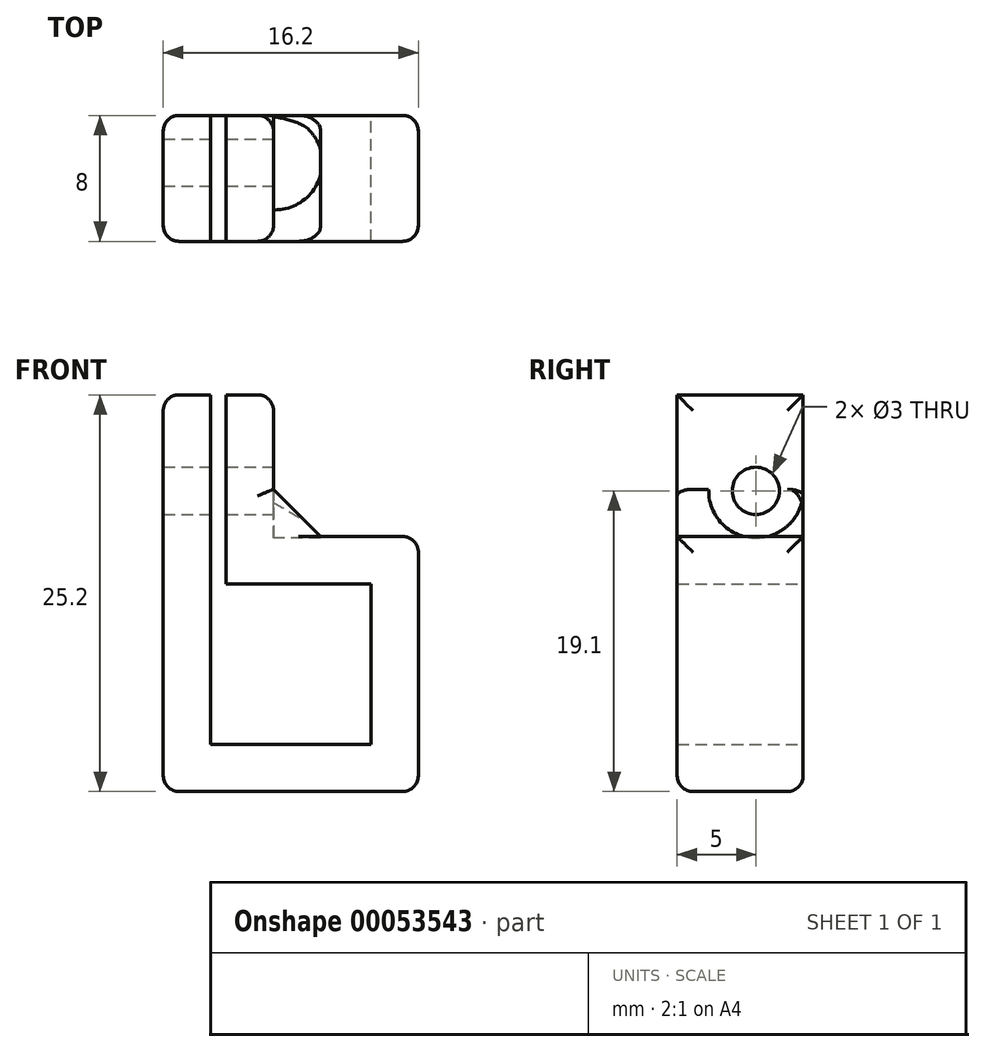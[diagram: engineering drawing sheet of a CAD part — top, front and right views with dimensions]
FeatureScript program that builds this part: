
annotation { "Feature Type Name" : "Feature", "Feature Type Description" : "" }
export const myFeature = defineFeature(function(context is Context, id is Id, definition is map)
    precondition{}
    {
        {
            var Q0;
            Q0=qCreatedBy(makeId("Front.planeOp"),FACE);
            var sketch = newSketch(context, id + "F0", { "sketchPlane" : qUnion([Q0])});
            skLineSegment(sketch, "E0.rect.bottom", {"start": v(5.1, -5.1) * mm, "end": v(-5.1, -5.1) * mm});
            skLineSegment(sketch, "E0.rect.top", {"start": v(5.1, 5.1) * mm, "end": v(-4.1, 5.1) * mm});
            skLineSegment(sketch, "E0.rect.left", {"start": v(5.1, -5.1) * mm, "end": v(5.1, 5.1) * mm});
            skLineSegment(sketch, "E0.rect.right", {"start": v(-5.1, -5.1) * mm, "end": v(-5.1, 5.1) * mm});
            skPoint(sketch, "E0.rect.middle", {"position": v(0, 0) * mm});
            skLineSegment(sketch, "E1.0", {"start": v(8.1, 8.1) * mm, "end": v(-1.1, 8.1) * mm});
            skLineSegment(sketch, "E1.1", {"start": v(8.1, -8.1) * mm, "end": v(8.1, 8.1) * mm});
            skLineSegment(sketch, "E1.2", {"start": v(8.1, -8.1) * mm, "end": v(-8.1, -8.1) * mm});
            skLineSegment(sketch, "E1.3", {"start": v(-8.1, -8.1) * mm, "end": v(-8.1, 8.1) * mm});
            skLineSegment(sketch, "E2", {"start": v(-8.1, 8.1) * mm, "end": v(-8.1, 17.1) * mm});
            skLineSegment(sketch, "E3", {"start": v(-8.1, 17.1) * mm, "end": v(-5.1, 17.1) * mm});
            skLineSegment(sketch, "E4", {"start": v(-5.1, 17.1) * mm, "end": v(-5.1, 8.1) * mm});
            skLineSegment(sketch, "E5", {"start": v(-4.1, 8.1) * mm, "end": v(-4.1, 17.1) * mm});
            skLineSegment(sketch, "E6", {"start": v(-4.1, 17.1) * mm, "end": v(-1.1, 17.1) * mm});
            skLineSegment(sketch, "E7", {"start": v(-1.1, 17.1) * mm, "end": v(-1.1, 8.1) * mm});
            skLineSegment(sketch, "E8", {"start": v(-5.1, 5.1) * mm, "end": v(-5.1, 8.1) * mm});
            skLineSegment(sketch, "E9", {"start": v(-4.1, 8.1) * mm, "end": v(-4.1, 5.1) * mm});
            skSolve(sketch);
        }
        {
            var Q0;
            Q0=qSketchRegion(id+"F0",true);
            extrude(context, id + "F1", {"entities" : qUnion([Q0]), "depth" : 8 * mm});
        }
        {
            var Q0;
            Q0=makeQuery(id+"F1.opExtrude","SWEPT_FACE",FACE,{"disambiguationData":[OSD([sQuery(id+"F0.wireOp",EDGE,"E7")])]});
            var sketch = newSketch(context, id + "F2", { "sketchPlane" : qUnion([Q0])});
            skCircle(sketch, "E10", {"center": v(-3, 11) * mm, "radius": 1.5 * mm});
            skPoint(sketch, "E10.centerSnap0", {"position": v(-7, 11) * mm});
            skPoint(sketch, "E10.centerSnap1", {"position": v(-3, 15.5) * mm});
            skSolve(sketch);
        }
        {
            var Q0;
            Q0=qSketchRegion(id+"F2",true);
            extrude(context, id + "F3", {"entities" : qUnion([Q0]), "operationType" : NewBodyOperationType.REMOVE, "endBound" : BoundingType.THROUGH_ALL, "oppositeDirection" : true, "depth" : 25 * mm});
        }
        {
            var Q0;
            Q0=makeQuery(id+"F1.opExtrude","SWEPT_EDGE",EDGE,{"disambiguationData":[OSD([sQuery(id+"F0.wireOp",EDGE,"E1.0"),sQuery(id+"F0.wireOp",EDGE,"E7")])]});
            chamfer(context, id + "F4", {"entities" : qUnion([Q0]), "width" : 3 * mm, "tangentPropagation" : true});
        }
        {
            var Q0;
            Q0=makeQuery(id+"F1.opExtrude","SWEPT_FACE",FACE,{"disambiguationData":[OSD([sQuery(id+"F0.wireOp",EDGE,"E1.1")])]});
            var Q1;
            Q1=makeQuery(id+"F1.opExtrude","SWEPT_FACE",FACE,{"disambiguationData":[OSD([sQuery(id+"F0.wireOp",EDGE,"E1.2")])]});
            var Q2;
            Q2=makeQuery(id+"F1.opExtrude","SWEPT_EDGE",EDGE,{"disambiguationData":[OSD([sQuery(id+"F0.wireOp",EDGE,"E2"),sQuery(id+"F0.wireOp",EDGE,"E3")])]});
            var Q3;
            Q3=makeQuery(id+"F1.opExtrude","CAP_EDGE",EDGE,{"disambiguationData":[OSD([sQuery(id+"F0.wireOp",EDGE,"E1.3"),sQuery(id+"F0.wireOp",EDGE,"E2")])],"isStart":true});
            var Q4;
            Q4=makeQuery(id+"F1.opExtrude","CAP_EDGE",EDGE,{"disambiguationData":[OSD([sQuery(id+"F0.wireOp",EDGE,"E1.3"),sQuery(id+"F0.wireOp",EDGE,"E2")])],"isStart":false});
            var Q5;
            Q5=makeQuery(id+"F1.opExtrude","SWEPT_EDGE",EDGE,{"disambiguationData":[OSD([sQuery(id+"F0.wireOp",EDGE,"E6"),sQuery(id+"F0.wireOp",EDGE,"E7")])]});
            var Q6;
            Q6=makeQuery(id+"F1.opExtrude","CAP_EDGE",EDGE,{"disambiguationData":[OSD([sQuery(id+"F0.wireOp",EDGE,"E7")])],"isStart":true});
            var Q7;
            Q7=makeQuery(id+"F1.opExtrude","CAP_EDGE",EDGE,{"disambiguationData":[OSD([sQuery(id+"F0.wireOp",EDGE,"E7")])],"isStart":false});
            fillet(context, id + "F5", {"entities" : qUnion([Q0, Q1, Q2, Q3, Q4, Q5, Q6, Q7]), "radius" : 1 * mm, "tangentPropagation" : true, "allowEdgeOverflow" : false});
        }
        {
            var Q0;
            {var subQ0=sQuery(id+"F0.wireOp",EDGE,"E7");var subQ1=sQuery(id+"F0.wireOp",EDGE,"E1.0");Q0=makeQuery(id+"F4.opChamfer","BLEND_EDGE",EDGE,{"blendedFrom":[makeQuery(id+"F1.opExtrude","SWEPT_EDGE",EDGE,{"disambiguationData":[OSD([subQ1,subQ0])]}),makeQuery(id+"F1.opExtrude","CAP_FACE",FACE,{"disambiguationData":[OSD([sQuery(id+"F0.wireOp",EDGE,"E0.rect.bottom"),sQuery(id+"F0.wireOp",EDGE,"E0.rect.top"),sQuery(id+"F0.wireOp",EDGE,"E0.rect.left"),sQuery(id+"F0.wireOp",EDGE,"E0.rect.right"),subQ1,sQuery(id+"F0.wireOp",EDGE,"E1.1"),sQuery(id+"F0.wireOp",EDGE,"E1.2"),sQuery(id+"F0.wireOp",EDGE,"E1.3"),sQuery(id+"F0.wireOp",EDGE,"E2"),sQuery(id+"F0.wireOp",EDGE,"E3"),sQuery(id+"F0.wireOp",EDGE,"E4"),sQuery(id+"F0.wireOp",EDGE,"E5"),sQuery(id+"F0.wireOp",EDGE,"E6"),subQ0,sQuery(id+"F0.wireOp",EDGE,"E8"),sQuery(id+"F0.wireOp",EDGE,"E9")])],"isStart":true})],"blendedInto":[makeQuery(id+"F1.opExtrude","CAP_FACE",FACE,{"disambiguationData":[OSD([sQuery(id+"F0.wireOp",EDGE,"E0.rect.bottom"),sQuery(id+"F0.wireOp",EDGE,"E0.rect.top"),sQuery(id+"F0.wireOp",EDGE,"E0.rect.left"),sQuery(id+"F0.wireOp",EDGE,"E0.rect.right"),subQ1,sQuery(id+"F0.wireOp",EDGE,"E1.1"),sQuery(id+"F0.wireOp",EDGE,"E1.2"),sQuery(id+"F0.wireOp",EDGE,"E1.3"),sQuery(id+"F0.wireOp",EDGE,"E2"),sQuery(id+"F0.wireOp",EDGE,"E3"),sQuery(id+"F0.wireOp",EDGE,"E4"),sQuery(id+"F0.wireOp",EDGE,"E5"),sQuery(id+"F0.wireOp",EDGE,"E6"),subQ0,sQuery(id+"F0.wireOp",EDGE,"E8"),sQuery(id+"F0.wireOp",EDGE,"E9")])],"isStart":true})]});}
            var Q1;
            {var subQ0=sQuery(id+"F0.wireOp",EDGE,"E7");var subQ1=sQuery(id+"F0.wireOp",EDGE,"E1.0");Q1=makeQuery(id+"F4.opChamfer","BLEND_EDGE",EDGE,{"blendedFrom":[makeQuery(id+"F1.opExtrude","SWEPT_EDGE",EDGE,{"disambiguationData":[OSD([subQ1,subQ0])]}),makeQuery(id+"F1.opExtrude","CAP_FACE",FACE,{"disambiguationData":[OSD([sQuery(id+"F0.wireOp",EDGE,"E0.rect.bottom"),sQuery(id+"F0.wireOp",EDGE,"E0.rect.top"),sQuery(id+"F0.wireOp",EDGE,"E0.rect.left"),sQuery(id+"F0.wireOp",EDGE,"E0.rect.right"),subQ1,sQuery(id+"F0.wireOp",EDGE,"E1.1"),sQuery(id+"F0.wireOp",EDGE,"E1.2"),sQuery(id+"F0.wireOp",EDGE,"E1.3"),sQuery(id+"F0.wireOp",EDGE,"E2"),sQuery(id+"F0.wireOp",EDGE,"E3"),sQuery(id+"F0.wireOp",EDGE,"E4"),sQuery(id+"F0.wireOp",EDGE,"E5"),sQuery(id+"F0.wireOp",EDGE,"E6"),subQ0,sQuery(id+"F0.wireOp",EDGE,"E8"),sQuery(id+"F0.wireOp",EDGE,"E9")])],"isStart":false})],"blendedInto":[makeQuery(id+"F1.opExtrude","CAP_FACE",FACE,{"disambiguationData":[OSD([sQuery(id+"F0.wireOp",EDGE,"E0.rect.bottom"),sQuery(id+"F0.wireOp",EDGE,"E0.rect.top"),sQuery(id+"F0.wireOp",EDGE,"E0.rect.left"),sQuery(id+"F0.wireOp",EDGE,"E0.rect.right"),subQ1,sQuery(id+"F0.wireOp",EDGE,"E1.1"),sQuery(id+"F0.wireOp",EDGE,"E1.2"),sQuery(id+"F0.wireOp",EDGE,"E1.3"),sQuery(id+"F0.wireOp",EDGE,"E2"),sQuery(id+"F0.wireOp",EDGE,"E3"),sQuery(id+"F0.wireOp",EDGE,"E4"),sQuery(id+"F0.wireOp",EDGE,"E5"),sQuery(id+"F0.wireOp",EDGE,"E6"),subQ0,sQuery(id+"F0.wireOp",EDGE,"E8"),sQuery(id+"F0.wireOp",EDGE,"E9")])],"isStart":false})]});}
            fillet(context, id + "F6", {"entities" : qUnion([Q0, Q1]), "radius" : 1 * mm, "tangentPropagation" : true, "allowEdgeOverflow" : false});
        }
        {
            var Q0;
            Q0=makeQuery(id+"F1.opExtrude","SWEPT_FACE",FACE,{"disambiguationData":[OSD([sQuery(id+"F0.wireOp",EDGE,"E7")])]});
            var sketch = newSketch(context, id + "F7", { "sketchPlane" : qUnion([Q0])});
            skCircle(sketch, "E11", {"center": v(-3, 11) * mm, "radius": 3 * mm});
            skSolve(sketch);
        }
        {
            var Q0;
            Q0=qSketchRegion(id+"F7",true);
            extrude(context, id + "F8", {"entities" : qUnion([Q0]), "operationType" : NewBodyOperationType.REMOVE, "depth" : 3 * mm});
        }
    });
